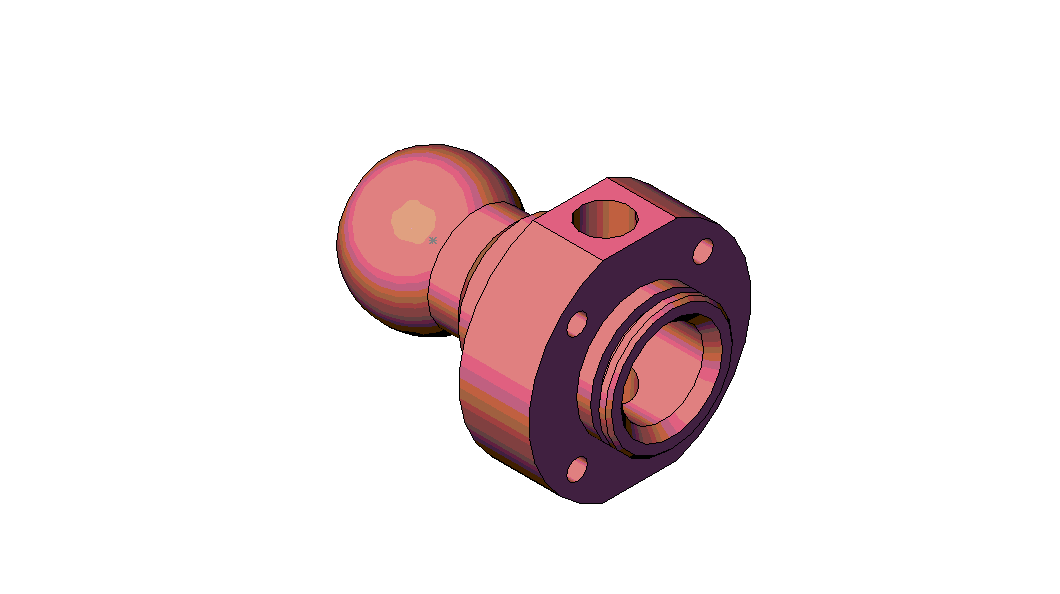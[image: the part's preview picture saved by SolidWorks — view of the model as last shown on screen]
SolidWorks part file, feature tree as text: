
SOLIDWORKS PART (.sldprt)
format: sldprt  version: not decoded by parser v0  size: 243,200 bytes
history: native  units: mm
features: sketch x5, plane x3, cut_extrude x3, material x1, revolve x1, pattern_circular x1, chamfer x1 + 1 further entry (+7 scaffold rows collapsed)
feature tree (23):
  scaffold x7  (default folders/planes/origin — collapsed)
  material  "Matériau <non spécifié>"
  "Corps de surface"
  plane  "Plan1"
  plane  "Plan2"
  plane  "Plan3"
  sketch  "Esquisse1"  dims[c1.D1=21.5mm c1.D2=14.0mm c1.D3=16.0mm c1.D4=38.0mm c1.D5=20.0mm c1.D6=5.0mm c2.D6=45.0deg c2.D7=22.0mm c2.D8=10.0mm c2.D9=2.6mm c2.D10=28.0mm c2.D11=3.0mm c2.D12=35.0mm c2.D13=20.0mm c2.D14=13.0mm c2.D15=10.1mm c2.D16=10.0mm c2.D17=68.0mm c2.D18=26.0mm c3.D18=45.0deg c3.D19=3.0mm c3.D20=~9.486833mm c4.D20=45.0deg c4.D21=45.9mm c5.D21=45.0deg c5.D22=13.25mm c5.D23=3.0mm c5.D24=4.0mm]
  revolve  "Base-Révolution"  Angle=360deg
  sketch  "Esquisse2"  dims[D1=66.0mm]
  cut_extrude  "Enlèv. mat.-Extru.1"  Depth=100mm
  sketch  "Esquisse3"  dims[D1=14.95mm D2=11.0mm]
  cut_extrude  "Enlèv. mat.-Extru.2"  [1 undecoded]
  sketch  "Esquisse4"  dims[c1.D2=6.5mm c1.D1=39.0mm c2.D1=45.0deg c2.D3=28.0mm]
  cut_extrude  "Enlèv. mat.-Extru.3"  [1 undecoded]
  pattern_circular  "Répétition circulaire1"  Count=4 Angle=90deg
  sketch  "Esquisse5"  dims[D1=14.0mm]
  chamfer  "Chanfrein1"  Distance=1mm Angle=45deg
decode coverage: 9 of 11 modeling features carry decoded parameters; 1 rows unclassified (native names shown)
note: ~ marks probable driven/reference dimensions
note: 2 parameter values undecoded
note: suppression state not decoded; provenance and decode notes live in map.json
